# Revit family: equip-sink-elkay-wash-snsr-wall-ewsf390263
name_source: partatom
category: Plumbing Fixtures
units: mm (PartAtom-declared; Revit-internal decimal feet)

## family parameters
Cut with Voids When Loaded = No
Host = Face
Part Type = Normal
Room Calculation Point = No
Round Connector Dimension = Use Radius
Shared = No

## types (1)
- equip-sink-elkay-wash-snsr-wall-EWSF390263
    AC Power = Yes
    Assembly Code = D2010410
    Backsplash Height = 0' - 4"
    Backsplash Width = 0' - 4 3/4"
    Bowl Bottom Width = 0' - 5 3/4"
    Bowl Depth = 0' - 11"
    Bowl Drain Location FB = 0' - 3 1/4"
    Bowl Length = 7' - 2"
    Bowl Width = 1' - 4 1/4"
    Bracket Front from Wall = 1' - 2"
    Bubbler CW Flow Rate = 2 GPM
    Bubbler Material = Metal - Steel - Stainless - Chrome
    Bubbler Nominal Dia = 0' - 0 1/2"
    Bubbler Nominal Radius = 0' - 0 1/4"
    CW Flow Rate = 2 GPM
    CWFU = 0
    Cost = 1 $
    Default Elevation = 3' - 0"
    Description = Wash-Up Lavatory Sinks
    Drain CL LR to Left Bowl Edge = 3' - 7"
    Drain Material = Metal - Steel - Stainless - Chrome
    Drain Pipe Extension = 0' - 0 1/4"
    EWSF 2D Line = Yes
    Faucet 1 CL Horiz to Valve Inlet 1 CL = 0' - 0 1/16"
    Faucet 1 CL to Sanitary Rough-In 1 = 0' - 2"
    Faucet 1 Hole A Front = 0' - 0 1/8"
    Faucet 1 Hole A Top = 0' - 0 1/4"
    Faucet 1 Hole A to Rough-In Water Supply CL 1 = 0' - 0"
    Faucet 1 Rough-In Water Supply CL Separation = 0' - 8"
    Faucet 2 CL Horiz to Valve Inlet 2 CL = 0' - 0 1/16"
    Faucet 2 Hole A From CL = 0' - 0"
    Faucet 2 Hole A Front = 0' - 0 1/8"
    Faucet 2 Hole A Top = 0' - 0 1/4"
    Faucet 2 Hole A to Rough-In Water Supply CL 2 = 0' - 0"
    Faucet 2 Rough-In Water Supply CL Separation = 0' - 8"
    Faucet 3 CL to Sanitary Rough-In 3 = 0' - 2"
    Faucet 3 Hole A From CL = 0' - 4"
    Faucet 3 Hole A Front = 0' - 0 1/8"
    Faucet 3 Hole A Top = 0' - 0 1/8"
    Faucet 3 Hole A from CL = 0' - 4"
    Faucet 4 Hole A Front = 0' - 0 1/8"
    Faucet 4 Hole A Top = 0' - 0 1/4"
    Faucet 4 Hole A to Rough-In Water Supply CL 4 = 0' - 0"
    Faucet 4 Rough-In Water Supply CL Separation = 0' - 8"
    Faucet CL From Back Backsplash = 0' - 2 3/8"
    Faucet CL Horiz to Control Box Inlet = 0' - 0 1/16"
    Faucet CL Vert to Bottom of Control Box Inlet = 1' - 2 5/8"
    Faucet CL to AC Adapter = 0' - 7"
    Faucet CL to AC Adapter Elev = 1' - 10"
    Faucet CL to Top Backsplash = 0' - 2"
    Faucet CL to Wall = 0' - 2 3/8"
    Faucet Hole Dia = 0' - 1 1/2"
    Faucet Hole One = No
    Faucet Hole Three = No
    Faucet Hole Two = No
    Faucet Material = Metal - Steel - Stainless - Chrome
    Faucet Part = LKB721C
    Faucet Water Supply Radius = 0' - 0 3/16"
    HW Flow Rate = 2 GPM
    HWFU = 0
    Handle Horiz Ref at Door = 0' - 2 25/32"
    Handle Horiz Ref at Handle Face = 0' - 0 19/32"
    Handle Vert Ref At Handle Face = 0' - 0 15/32"
    Handle Vert Ref at Door = 0' - 3 3/8"
    Hidden Length = 7' - 6"
    Hidden Width = 1' - 11"
    Hole Radius = 0' - 0 3/4"
    Keynote = D2010410
    Manufacturer = Elkay Manufacturing
    MasterFormat Number = 22.42.16.16
    MasterFormat Title = Commercial Sinks
    Mechanical Mix Valve = No
    Model = EWSF390263
    No Mix Valve = No
    Nominal Dia = 0' - 0 1/2"
    Nominal Radius = 0' - 0 1/4"
    OmniClass Code = 23.45.05.14.14.27
    OmniClass Title = Service Sinks
    Overhang Width = 0' - 1"
    Overhead Depth Back Angle Edge = 0' - 4 1/32"
    Overhead Depth Front Edge = 0' - 4"
    Rough-In Sanitary Installation Height = 1' - 10"
    Rough-In Sanitary Left From CL Sink = 0' - 2"
    Rough-In Water Supply Installation Height = 1' - 4 1/2"
    Sanitary Flow Rate = 10 GPM
    Sanitary Nominal Dia = 0' - 1 1/2"
    Sanitary Nominal Radius = 0' - 0 3/4"
    Side Splashes = No
    Sink Bottom Front Corner From Back = 0' - 10 1/2"
    Sink Depth = 2' - 2"
    Sink Edge Left to Faucet 1 Hole A = 1' - 4"
    Sink Edge Right to Faucet 4 Hole A = 1' - 4"
    Sink Edge to Drain 1 Left CL = 1' - 4"
    Sink Edge to Drain 4 Left CL = 1' - 4"
    Sink Length = 7' - 6"
    Sink Material = Metal - Steel - Stainless - Chrome
    Sink Mid Angle Pt From Rim = 0' - 7 1/4"
    Sink Mid Angle Pt from Front = 0' - 6 3/4"
    Sink Panel Angle Pt From Front = 1' - 6 1/4"
    Sink Part = EWSF390263
    Sink Rim Front Width = 0' - 2"
    Sink Rim Left Width = 0' - 2"
    Sink Rim Right Width = 0' - 2"
    Sink San Conn Extr Visibility = No
    Sink Width = 1' - 11"
    Specification Sheet URL = http://www.elkayusa.com
    Stem Material = Metal - Steel
    Supply Line Mix Length = 0' - 0 1/2"
    Thermostatic Mix Valve = No
    Toe Kick Depth = 0' - 1 1/2"
    Toe Kick Front Width = 0' - 8 7/16"
    URL = www.elkayusa.com
    Valve Material = Metal - Steel - Stainless - Chrome
    Vent Connection = Yes
    WFU = 0

## geometry (parser evidence)
native form markers: Sweep x9
no freeform markers — native parametric forms only
